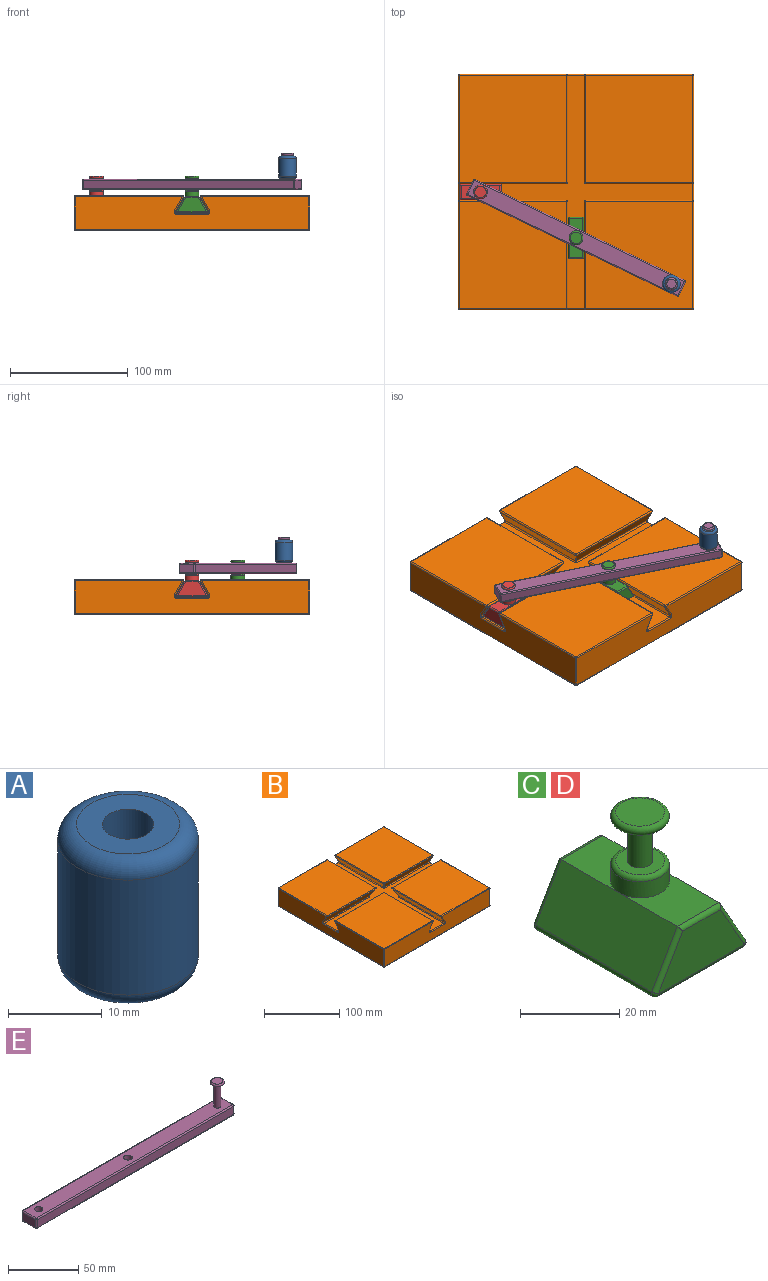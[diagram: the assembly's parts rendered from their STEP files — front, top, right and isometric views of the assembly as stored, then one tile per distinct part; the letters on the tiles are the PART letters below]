
ASSEMBLY  parts=5 mates=5
PART A: 6 faces, bbox 16.2x16.2x19 mm
  f0: cylinder r=2.75mm len=19mm, axis (0,0,-1), area 328.3mm2, adj f2,f3
  f1: cylinder r=7.5mm len=15mm, axis (0,0,-1), area 706.9mm2, adj f4,f5
  f2: plane 11x11mm, normal (0,0,1), area 71.3mm2, adj f0,f5
  f3: plane 11x11mm, normal (0,0,-1), area 71.3mm2, adj f0,f4
  f4: torus R=5.5mm, axis (0,0,1), area 133.7mm2, adj f1,f3
  f5: torus R=5.5mm, axis (0,0,1), area 133.7mm2, adj f1,f2
PART B: 98 faces, bbox 200x200x30 mm
  f0: plane 198x28mm, normal (0,-1,0), area 5177.4mm2, adj f55,f56,f63,f70,f71,f77,f84,f85
  f1: plane 198x28mm, normal (0,1,0), area 5177.4mm2, adj f28,f30,f34,f41,f42,f45,f58,f59
  f2: plane 198x28mm, normal (1,0,0), area 5177.4mm2, adj f21,f24,f25,f31,f39,f40,f57,f58
  f3: plane 198x198mm, normal (0,0,1), area 9806.4mm2, adj f18,f20,f23,f24,f34,f35,f46,f53
  f4: plane 198x28mm, normal (-1,0,0), area 5177.4mm2, adj f60,f67,f74,f75,f80,f86,f87,f91
  f5: plane 90.93x90.93mm, normal (0,0,1), area 8267.9mm2, adj f37,f38,f56,f57
  f6: plane 90.93x90.93mm, normal (0,0,1), area 8267.9mm2, adj f83,f92,f93,f97
  f7: plane 90.93x12mm, normal (0.87,0,-0.5), area 1211.9mm2, adj f42,f43,f52,f53
  f8: plane 90.93x12mm, normal (-0.87,0,-0.5), area 1211.9mm2, adj f19,f23,f27,f28
  f9: plane 90.93x90.93mm, normal (0,0,1), area 8267.9mm2, adj f26,f27,f40,f41
  f10: plane 90.93x90.93mm, normal (0,0,1), area 8267.9mm2, adj f43,f51,f59,f60
  f11: plane 198x198mm, normal (0,0,-1), area 39204mm2, adj f72,f73,f85,f86
  f12: plane 90.93x12mm, normal (0.87,0,-0.5), area 1211.9mm2, adj f69,f82,f83,f84
  f13: plane 90.93x12mm, normal (-0.87,0,-0.5), area 1211.9mm2, adj f36,f37,f54,f55
  f14: plane 90.93x12mm, normal (0,0.87,-0.5), area 1211.9mm2, adj f35,f36,f38,f39
  f15: plane 90.93x12mm, normal (0,-0.87,-0.5), area 1211.9mm2, adj f18,f19,f25,f26
  f16: plane 90.93x12mm, normal (0,-0.87,-0.5), area 1211.9mm2, adj f51,f52,f67,f68
  f17: plane 90.93x12mm, normal (0,0.87,-0.5), area 1211.9mm2, adj f81,f82,f91,f92
  f18: cylinder r=1mm len=84mm, axis (1,0,0), area 175.9mm2, adj f3,f15,f20,f21
  f19: cylinder r=1mm len=12.13mm, axis (-0.45,-0.45,0.77), area 20.1mm2, adj f8,f15,f20,f22
  f20: bspline ~1.73x1.73mm, area 3.5mm2, adj f3,f18,f19,f23
  f21: torus R=2mm, axis (1,0,0), area 4.5mm2, adj f2,f18,f24,f25
  f22: sphere r=1mm, area 2.5mm2, adj f19,f26,f27
  f23: cylinder r=1mm len=84mm, axis (0,1,0), area 175.9mm2, adj f3,f8,f20,f30
  f24: cylinder r=1mm len=26.54mm, axis (0,-1,0), area 41.7mm2, adj f2,f3,f21,f31
  f25: cylinder r=1mm len=12.5mm, axis (0,0.5,-0.87), area 21.8mm2, adj f2,f15,f21,f32
  f26: cylinder r=1mm len=90.93mm, axis (1,0,0), area 190.4mm2, adj f9,f15,f22,f32
  f27: cylinder r=1mm len=90.93mm, axis (0,1,0), area 190.4mm2, adj f8,f9,f22,f33
  f28: cylinder r=1mm len=12.5mm, axis (-0.5,0,0.87), area 21.8mm2, adj f1,f8,f30,f33
  f29: sphere r=1mm, area 2.5mm2, adj f36,f37,f38
  f30: torus R=2mm, axis (0,1,0), area 4.5mm2, adj f1,f23,f28,f34
  f31: torus R=2mm, axis (1,0,0), area 4.5mm2, adj f2,f24,f35,f39
  f32: sphere r=1mm, area 2.1mm2, adj f25,f26,f40
  f33: sphere r=1mm, area 2.1mm2, adj f27,f28,f41
  f34: cylinder r=1mm len=26.54mm, axis (1,0,0), area 41.7mm2, adj f1,f3,f30,f45
  f35: cylinder r=1mm len=84mm, axis (1,0,0), area 175.9mm2, adj f3,f14,f31,f46
  f36: cylinder r=1mm len=12.13mm, axis (0.45,-0.45,-0.77), area 20.1mm2, adj f13,f14,f29,f46
  f37: cylinder r=1mm len=90.93mm, axis (0,1,0), area 190.4mm2, adj f5,f13,f29,f47
  f38: cylinder r=1mm len=90.93mm, axis (1,0,0), area 190.4mm2, adj f5,f14,f29,f48
  f39: cylinder r=1mm len=12.5mm, axis (0,0.5,0.87), area 21.8mm2, adj f2,f14,f31,f48
  f40: cylinder r=1mm len=90.93mm, axis (0,-1,0), area 142.8mm2, adj f2,f9,f32,f49
  f41: cylinder r=1mm len=90.93mm, axis (1,0,0), area 142.8mm2, adj f1,f9,f33,f49
  f42: cylinder r=1mm len=12.5mm, axis (-0.5,0,-0.87), area 21.8mm2, adj f1,f7,f45,f50
  f43: cylinder r=1mm len=90.93mm, axis (0,1,0), area 190.4mm2, adj f7,f10,f44,f50
  f44: sphere r=1mm, area 2.5mm2, adj f43,f51,f52
  f45: torus R=2mm, axis (0,1,0), area 4.5mm2, adj f1,f34,f42,f53
  f46: bspline ~1.73x1.73mm, area 3.5mm2, adj f3,f35,f36,f54
  f47: sphere r=1mm, area 2.1mm2, adj f37,f55,f56
  f48: sphere r=1mm, area 2.1mm2, adj f38,f39,f57
  f49: sphere r=1mm, area 1.6mm2, adj f40,f41,f58
  f50: sphere r=1mm, area 2.1mm2, adj f42,f43,f59
  f51: cylinder r=1mm len=90.93mm, axis (1,0,0), area 190.4mm2, adj f10,f16,f44,f61
  f52: cylinder r=1mm len=12.13mm, axis (-0.45,0.45,-0.77), area 20.1mm2, adj f7,f16,f44,f62
  f53: cylinder r=1mm len=84mm, axis (0,1,0), area 175.9mm2, adj f3,f7,f45,f62
  f54: cylinder r=1mm len=84mm, axis (0,1,0), area 175.9mm2, adj f3,f13,f46,f63
  f55: cylinder r=1mm len=12.5mm, axis (-0.5,0,0.87), area 21.8mm2, adj f0,f13,f47,f63
  f56: cylinder r=1mm len=90.93mm, axis (-1,0,0), area 142.8mm2, adj f0,f5,f47,f64
  f57: cylinder r=1mm len=90.93mm, axis (0,-1,0), area 142.8mm2, adj f2,f5,f48,f64
  f58: cylinder r=1mm len=28mm, axis (0,0,-1), area 44mm2, adj f1,f2,f49,f65
  f59: cylinder r=1mm len=90.93mm, axis (1,0,0), area 142.8mm2, adj f1,f10,f50,f66
  f60: cylinder r=1mm len=90.93mm, axis (0,1,0), area 142.8mm2, adj f4,f10,f61,f66
  f61: sphere r=1mm, area 2.1mm2, adj f51,f60,f67
  f62: bspline ~1.73x1.73mm, area 3.5mm2, adj f3,f52,f53,f68
  f63: torus R=2mm, axis (0,1,0), area 4.5mm2, adj f0,f54,f55,f70
  f64: sphere r=1mm, area 1.6mm2, adj f56,f57,f71
  f65: sphere r=1mm, area 1.6mm2, adj f58,f72,f73
  f66: sphere r=1mm, area 1.6mm2, adj f59,f60,f74
  f67: cylinder r=1mm len=12.5mm, axis (0,0.5,-0.87), area 21.8mm2, adj f4,f16,f61,f75
  f68: cylinder r=1mm len=84mm, axis (1,0,0), area 175.9mm2, adj f3,f16,f62,f75
  f69: cylinder r=1mm len=84mm, axis (0,1,0), area 175.9mm2, adj f3,f12,f76,f77
  f70: cylinder r=1mm len=26.54mm, axis (1,0,0), area 41.7mm2, adj f0,f3,f63,f77
  f71: cylinder r=1mm len=28mm, axis (0,0,1), area 44mm2, adj f0,f2,f64,f78
  f72: cylinder r=1mm len=198mm, axis (0,1,0), area 311mm2, adj f2,f11,f65,f78
  f73: cylinder r=1mm len=198mm, axis (-1,0,0), area 311mm2, adj f1,f11,f65,f79
  f74: cylinder r=1mm len=28mm, axis (0,0,1), area 44mm2, adj f1,f4,f66,f79
  f75: torus R=2mm, axis (1,0,0), area 4.5mm2, adj f4,f67,f68,f80
  f76: bspline ~1.73x1.73mm, area 3.5mm2, adj f3,f69,f81,f82
  f77: torus R=2mm, axis (0,1,0), area 4.5mm2, adj f0,f69,f70,f84
  f78: sphere r=1mm, area 1.6mm2, adj f71,f72,f85
  f79: sphere r=1mm, area 1.6mm2, adj f73,f74,f86
  f80: cylinder r=1mm len=26.54mm, axis (0,-1,0), area 41.7mm2, adj f3,f4,f75,f87
  f81: cylinder r=1mm len=84mm, axis (1,0,0), area 175.9mm2, adj f3,f17,f76,f87
  f82: cylinder r=1mm len=12.13mm, axis (0.45,0.45,0.77), area 20.1mm2, adj f12,f17,f76,f88
  f83: cylinder r=1mm len=90.93mm, axis (0,1,0), area 190.4mm2, adj f6,f12,f88,f89
  f84: cylinder r=1mm len=12.5mm, axis (-0.5,0,-0.87), area 21.8mm2, adj f0,f12,f77,f89
  f85: cylinder r=1mm len=198mm, axis (1,0,0), area 311mm2, adj f0,f11,f78,f90
  f86: cylinder r=1mm len=198mm, axis (0,-1,0), area 311mm2, adj f4,f11,f79,f90
  f87: torus R=2mm, axis (1,0,0), area 4.5mm2, adj f4,f80,f81,f91
  f88: sphere r=1mm, area 2.5mm2, adj f82,f83,f92
  f89: sphere r=1mm, area 2.1mm2, adj f83,f84,f93
  f90: sphere r=1mm, area 1.6mm2, adj f85,f86,f94
  f91: cylinder r=1mm len=12.5mm, axis (0,0.5,0.87), area 21.8mm2, adj f4,f17,f87,f95
  f92: cylinder r=1mm len=90.93mm, axis (1,0,0), area 190.4mm2, adj f6,f17,f88,f95
  f93: cylinder r=1mm len=90.93mm, axis (-1,0,0), area 142.8mm2, adj f0,f6,f89,f96
  f94: cylinder r=1mm len=28mm, axis (0,0,-1), area 44mm2, adj f0,f4,f90,f96
  f95: sphere r=1mm, area 2.1mm2, adj f91,f92,f97
  f96: sphere r=1mm, area 1.6mm2, adj f93,f94,f97
  f97: cylinder r=1mm len=90.93mm, axis (0,1,0), area 142.8mm2, adj f4,f6,f95,f96
PART C: 28 faces, bbox 26.5x35x31 mm
  f0: plane 16.5x11.83mm, normal (0,0,1), area 140.3mm2, adj f5,f6,f7,f25
  f1: plane 24.54x12mm, normal (0,-1,0), area 211.3mm2, adj f14,f15,f17,f18
  f2: plane 16.5x11.83mm, normal (0,0,1), area 140.3mm2, adj f5,f6,f7,f15
  f3: plane 24.54x12mm, normal (0,1,0), area 211.3mm2, adj f22,f24,f25,f27
  f4: plane 33x24.54mm, normal (0,0,-1), area 809.7mm2, adj f18,f19,f23,f24
  f5: plane 33x12.5mm, normal (0.87,0,0.5), area 476.3mm2, adj f0,f2,f14,f19,f22
  f6: plane 33x12.5mm, normal (-0.87,0,0.5), area 476.3mm2, adj f0,f2,f17,f23,f27
  f7: cylinder r=5.92mm len=11.83mm, axis (0,0,-1), area 148.7mm2, adj f0,f2,f13
  f8: plane 9.83x9.83mm, normal (0,0,1), area 56.3mm2, adj f9,f13
  f9: cylinder r=2.5mm len=10mm, axis (0,0,-1), area 157.1mm2, adj f8,f11
  f10: plane 9.83x9.83mm, normal (0,0,1), area 76mm2, adj f12
  f11: plane 9.83x9.83mm, normal (0,0,-1), area 56.3mm2, adj f9,f12
  f12: torus R=4.92mm, axis (0,0,1), area 109.6mm2, adj f10,f11
  f13: torus R=4.92mm, axis (0,0,1), area 54.8mm2, adj f7,f8
  f14: cylinder r=1mm len=13mm, axis (0.5,0,-0.87), area 22.3mm2, adj f1,f5,f15,f16
  f15: cylinder r=1mm len=11.83mm, axis (-1,0,0), area 17.9mm2, adj f1,f2,f14,f17
  f16: sphere r=1mm, area 2.1mm2, adj f14,f18,f19
  f17: cylinder r=1mm len=13mm, axis (0.5,0,0.87), area 22.3mm2, adj f1,f6,f15,f20
  f18: cylinder r=1mm len=24.54mm, axis (1,0,0), area 38.5mm2, adj f1,f4,f16,f20
  f19: cylinder r=1mm len=33mm, axis (0,-1,0), area 69.1mm2, adj f4,f5,f16,f21
  f20: sphere r=1mm, area 2.1mm2, adj f17,f18,f23
  f21: sphere r=1mm, area 2.1mm2, adj f19,f22,f24
  f22: cylinder r=1mm len=13mm, axis (0.5,0,-0.87), area 22.3mm2, adj f3,f5,f21,f25
  f23: cylinder r=1mm len=33mm, axis (0,-1,0), area 69.1mm2, adj f4,f6,f20,f26
  f24: cylinder r=1mm len=24.54mm, axis (-1,0,0), area 38.5mm2, adj f3,f4,f21,f26
  f25: cylinder r=1mm len=11.83mm, axis (1,0,0), area 17.9mm2, adj f0,f3,f22,f27
  f26: sphere r=1mm, area 2.1mm2, adj f23,f24,f27
  f27: cylinder r=1mm len=13mm, axis (0.5,0,0.87), area 22.3mm2, adj f3,f6,f25,f26
PART D: same geometry as C
PART E: 32 faces, bbox 200x15x31 mm
  f0: plane 198x7mm, normal (0,1,0), area 1386mm2, adj f20,f25,f28,f31
  f1: plane 13x7mm, normal (-1,0,0), area 91mm2, adj f17,f26,f27,f31
  f2: plane 198x7mm, normal (0,-1,0), area 1386mm2, adj f12,f16,f17,f18
  f3: cylinder r=3mm len=9mm, axis (0,0,-1), area 169.6mm2, adj f6,f7
  f4: cylinder r=3mm len=9mm, axis (0,0,-1), area 169.6mm2, adj f6,f7
  f5: plane 13x7mm, normal (1,0,0), area 91mm2, adj f12,f15,f19,f20
  f6: plane 198x13mm, normal (0,0,1), area 2497.8mm2, adj f3,f4,f8,f15,f16,f25,f26
  f7: plane 198x13mm, normal (0,0,-1), area 2517.5mm2, adj f3,f4,f18,f19,f27,f28
  f8: cylinder r=2.5mm len=20mm, axis (0,0,-1), area 314.2mm2, adj f6,f10
  f9: plane 8x8mm, normal (0,0,1), area 50.3mm2, adj f11
  f10: plane 8x8mm, normal (0,0,-1), area 30.6mm2, adj f8,f11
  f11: torus R=4mm, axis (0,0,1), area 91.5mm2, adj f9,f10
  f12: cylinder r=1mm len=7mm, axis (0,0,1), area 11mm2, adj f2,f5,f13,f14
  f13: sphere r=1mm, area 1.6mm2, adj f12,f15,f16
  f14: sphere r=1mm, area 1.6mm2, adj f12,f18,f19
  f15: cylinder r=1mm len=13mm, axis (0,-1,0), area 20.4mm2, adj f5,f6,f13,f21
  f16: cylinder r=1mm len=198mm, axis (-1,0,0), area 311mm2, adj f2,f6,f13,f22
  f17: cylinder r=1mm len=7mm, axis (0,0,-1), area 11mm2, adj f1,f2,f22,f23
  f18: cylinder r=1mm len=198mm, axis (1,0,0), area 311mm2, adj f2,f7,f14,f23
  f19: cylinder r=1mm len=13mm, axis (0,1,0), area 20.4mm2, adj f5,f7,f14,f24
  f20: cylinder r=1mm len=7mm, axis (0,0,-1), area 11mm2, adj f0,f5,f21,f24
  f21: sphere r=1mm, area 1.6mm2, adj f15,f20,f25
  f22: sphere r=1mm, area 1.6mm2, adj f16,f17,f26
  f23: sphere r=1mm, area 1.6mm2, adj f17,f18,f27
  f24: sphere r=1mm, area 1.6mm2, adj f19,f20,f28
  f25: cylinder r=1mm len=198mm, axis (1,0,0), area 311mm2, adj f0,f6,f21,f29
  f26: cylinder r=1mm len=13mm, axis (0,1,0), area 20.4mm2, adj f1,f6,f22,f29
  f27: cylinder r=1mm len=13mm, axis (0,-1,0), area 20.4mm2, adj f1,f7,f23,f30
  f28: cylinder r=1mm len=198mm, axis (-1,0,0), area 311mm2, adj f0,f7,f24,f30
  f29: sphere r=1mm, area 1.6mm2, adj f25,f26,f31
  f30: sphere r=1mm, area 1.6mm2, adj f27,f28,f31
  f31: cylinder r=1mm len=7mm, axis (0,0,1), area 11mm2, adj f0,f1,f29,f30
PLACE A rot(axis=(0,0,-1),52.7deg) t=(81.1,-78.05,44.5)mm
PLACE B at identity fixed
PLACE C t=(0,-39.03,15.5)mm
PLACE D rot(axis=(0,0,1),90deg) t=(-81.1,0,15.5)mm
PLACE E rot(axis=(0,0,-1),25.7deg) t=(0,-39.03,35)mm
MATE slider B.f2 <-> D.f1  axis (1,0,0) through (100,0,14)mm
MATE slider C.f1 <-> B.f0  axis (0,-1,0) through (0,-56.53,16.5)mm
MATE revolute E.f3 <-> C.f9  axis (0,0,-1) through (0,-39.03,39.5)mm
MATE revolute E.f4 <-> D.f9  axis (0,0,-1) through (-81.1,0,39.5)mm
MATE revolute A.f1 <-> E.f8  axis (0,0,-1) through (81.1,-78.05,54)mm
